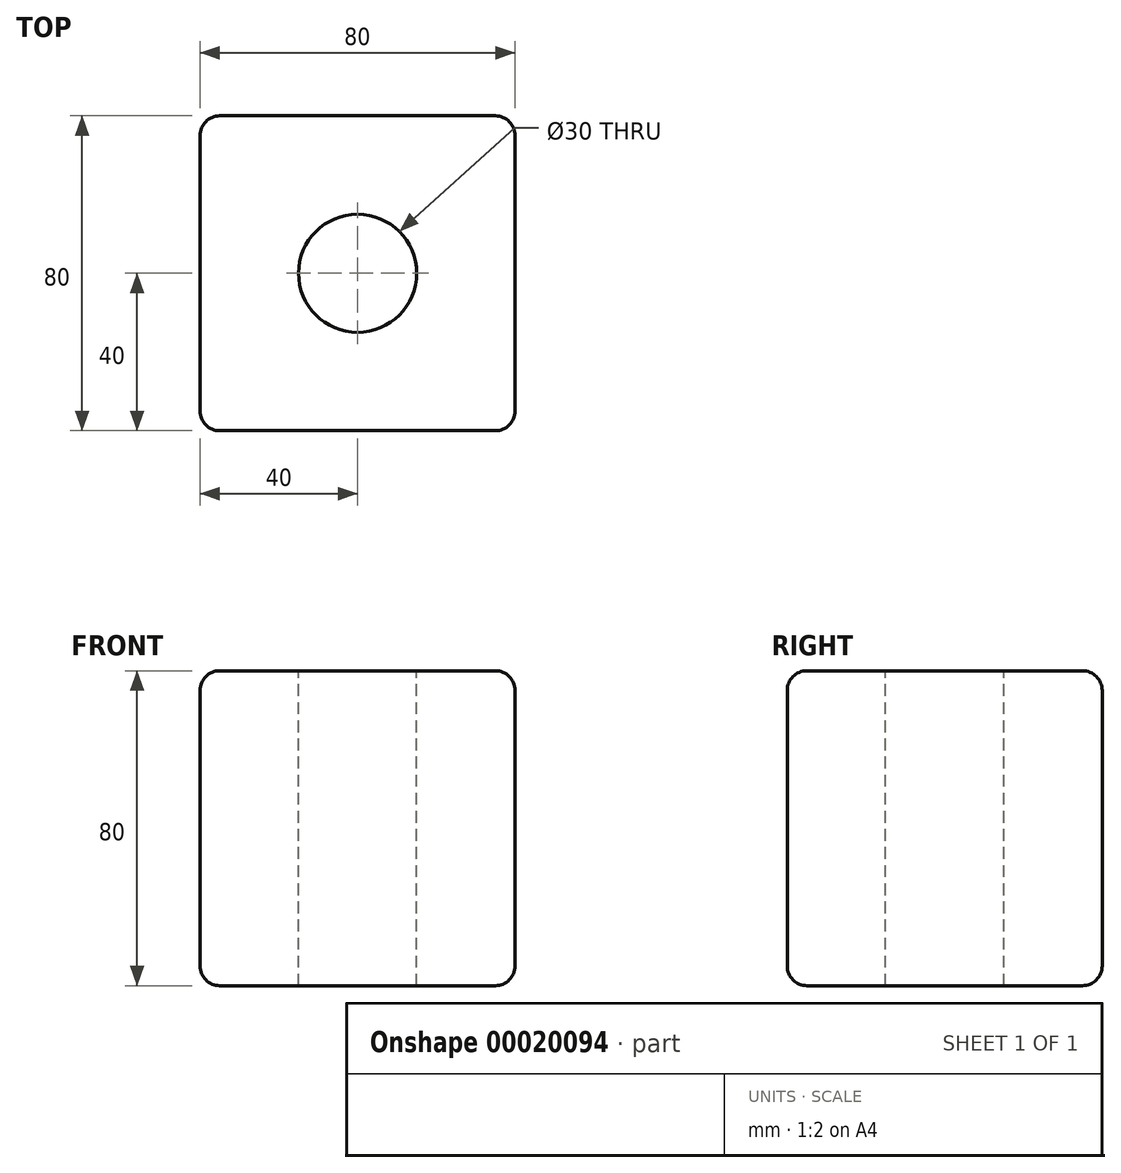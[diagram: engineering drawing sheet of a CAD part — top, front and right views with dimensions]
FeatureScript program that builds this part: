
annotation { "Feature Type Name" : "Feature", "Feature Type Description" : "" }
export const myFeature = defineFeature(function(context is Context, id is Id, definition is map)
    precondition{}
    {
        {
            var Q0;
            Q0=qCreatedBy(makeId("Top.planeOp"),FACE);
            var sketch = newSketch(context, id + "F0", { "sketchPlane" : qUnion([Q0])});
            skLineSegment(sketch, "E0.rect.bottom", {"start": v(-40, 40) * mm, "end": v(40, 40) * mm});
            skLineSegment(sketch, "E0.rect.top", {"start": v(-40, -40) * mm, "end": v(40, -40) * mm});
            skLineSegment(sketch, "E0.rect.left", {"start": v(-40, 40) * mm, "end": v(-40, -40) * mm});
            skLineSegment(sketch, "E0.rect.right", {"start": v(40, 40) * mm, "end": v(40, -40) * mm});
            skPoint(sketch, "E0.rect.middle", {"position": v(0, 0) * mm});
            skSolve(sketch);
        }
        {
            var Q0;
            Q0=makeQuery(id+"F0.imprint","IMPRINT",FACE,{"disambiguationData":[TD([[makeQuery(id+"F0.imprint","IMPRINT",EDGE,{"derivedFrom":sQuery(id+"F0.wireOp",EDGE,"E0.rect.bottom")}),-1.0]])]});
            extrude(context, id + "F1", {"entities" : qUnion([Q0]), "endBound" : BoundingType.SYMMETRIC, "depth" : 80 * mm});
        }
        {
            var Q0;
            Q0=makeQuery(id+"F1.opExtrude","SWEPT_EDGE",EDGE,{"disambiguationData":[OSD([sQuery(id+"F0.wireOp",EDGE,"E0.rect.bottom"),sQuery(id+"F0.wireOp",EDGE,"E0.rect.left")])]});
            var Q1;
            Q1=makeQuery(id+"F1.opExtrude","CAP_EDGE",EDGE,{"disambiguationData":[OSD([sQuery(id+"F0.wireOp",EDGE,"E0.rect.bottom")])],"isStart":false});
            var Q2;
            Q2=makeQuery(id+"F1.opExtrude","SWEPT_EDGE",EDGE,{"disambiguationData":[OSD([sQuery(id+"F0.wireOp",EDGE,"E0.rect.bottom"),sQuery(id+"F0.wireOp",EDGE,"E0.rect.right")])]});
            var Q3;
            Q3=makeQuery(id+"F1.opExtrude","CAP_EDGE",EDGE,{"disambiguationData":[OSD([sQuery(id+"F0.wireOp",EDGE,"E0.rect.bottom")])],"isStart":true});
            var Q4;
            Q4=makeQuery(id+"F1.opExtrude","CAP_EDGE",EDGE,{"disambiguationData":[OSD([sQuery(id+"F0.wireOp",EDGE,"E0.rect.left")])],"isStart":false});
            var Q5;
            Q5=makeQuery(id+"F1.opExtrude","CAP_EDGE",EDGE,{"disambiguationData":[OSD([sQuery(id+"F0.wireOp",EDGE,"E0.rect.left")])],"isStart":true});
            var Q6;
            Q6=makeQuery(id+"F1.opExtrude","CAP_EDGE",EDGE,{"disambiguationData":[OSD([sQuery(id+"F0.wireOp",EDGE,"E0.rect.right")])],"isStart":false});
            var Q7;
            Q7=makeQuery(id+"F1.opExtrude","CAP_EDGE",EDGE,{"disambiguationData":[OSD([sQuery(id+"F0.wireOp",EDGE,"E0.rect.top")])],"isStart":false});
            var Q8;
            Q8=makeQuery(id+"F1.opExtrude","SWEPT_EDGE",EDGE,{"disambiguationData":[OSD([sQuery(id+"F0.wireOp",EDGE,"E0.rect.top"),sQuery(id+"F0.wireOp",EDGE,"E0.rect.left")])]});
            var Q9;
            Q9=makeQuery(id+"F1.opExtrude","CAP_EDGE",EDGE,{"disambiguationData":[OSD([sQuery(id+"F0.wireOp",EDGE,"E0.rect.right")])],"isStart":true});
            var Q10;
            Q10=makeQuery(id+"F1.opExtrude","SWEPT_EDGE",EDGE,{"disambiguationData":[OSD([sQuery(id+"F0.wireOp",EDGE,"E0.rect.top"),sQuery(id+"F0.wireOp",EDGE,"E0.rect.right")])]});
            var Q11;
            Q11=makeQuery(id+"F1.opExtrude","CAP_EDGE",EDGE,{"disambiguationData":[OSD([sQuery(id+"F0.wireOp",EDGE,"E0.rect.top")])],"isStart":true});
            fillet(context, id + "F2", {"entities" : qUnion([Q0, Q1, Q2, Q3, Q4, Q5, Q6, Q7, Q8, Q9, Q10, Q11]), "radius" : 5 * mm, "allowEdgeOverflow" : false});
        }
        {
            var Q0;
            Q0=makeQuery(id+"F1.opExtrude","CAP_FACE",FACE,{"disambiguationData":[OSD([sQuery(id+"F0.wireOp",EDGE,"E0.rect.bottom"),sQuery(id+"F0.wireOp",EDGE,"E0.rect.top"),sQuery(id+"F0.wireOp",EDGE,"E0.rect.left"),sQuery(id+"F0.wireOp",EDGE,"E0.rect.right")])],"isStart":false});
            var sketch = newSketch(context, id + "F3", { "sketchPlane" : qUnion([Q0])});
            skCircle(sketch, "E1", {"center": v(0, 0) * mm, "radius": 15 * mm});
            skSolve(sketch);
        }
        {
            var Q0;
            Q0=makeQuery(id+"F3.imprint","IMPRINT",FACE,{"disambiguationData":[TD([[makeQuery(id+"F3.imprint","IMPRINT",EDGE,{"derivedFrom":sQuery(id+"F3.wireOp",EDGE,"E1")}),1.0]])]});
            extrude(context, id + "F4", {"entities" : qUnion([Q0]), "operationType" : NewBodyOperationType.REMOVE, "endBound" : BoundingType.THROUGH_ALL, "oppositeDirection" : true, "depth" : 25 * mm});
        }
    });
